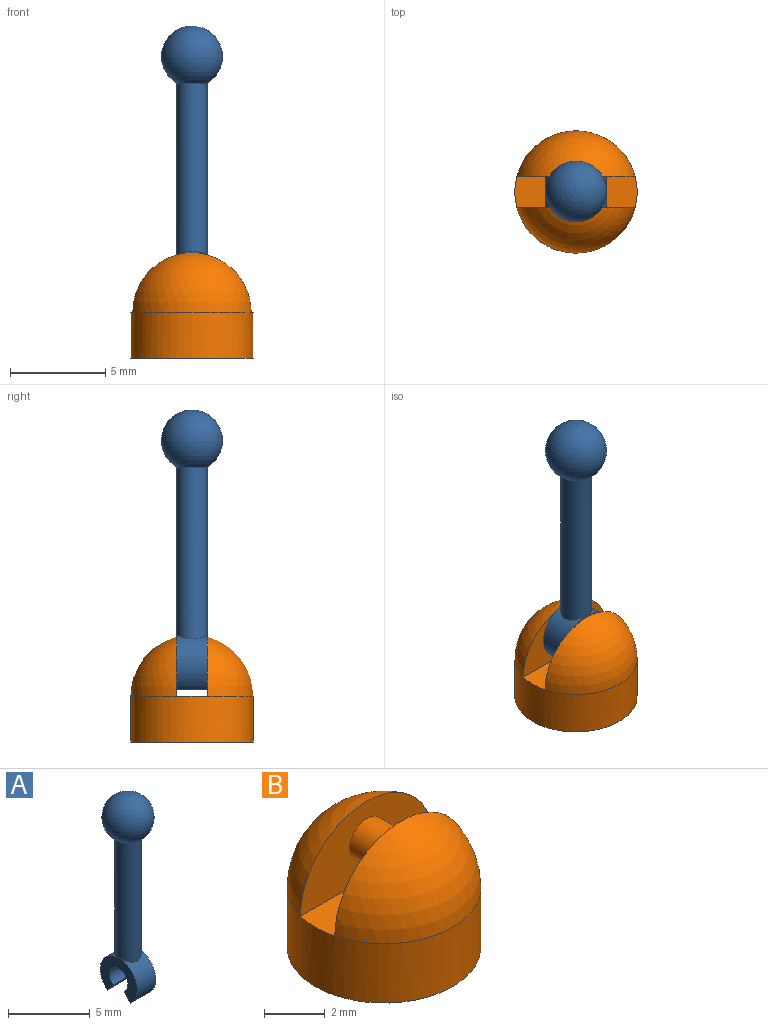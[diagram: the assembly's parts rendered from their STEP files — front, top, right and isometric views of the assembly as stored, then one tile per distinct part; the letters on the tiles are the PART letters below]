
ASSEMBLY  parts=2 mates=1
PART A: 9 faces, bbox 3.2x3.2x14.7 mm
  f0: cylinder r=1.6mm len=2.87mm, axis (-1,0,0), area 5.3mm2, adj f4,f5,f6,f7
  f1: cylinder r=1.6mm len=2.87mm, axis (-1,0,0), area 5.3mm2, adj f2,f5,f6,f7
  f2: plane 1.6x0.63mm, normal (0,0.79,-0.61), area 1.3mm2, adj f1,f3,f5,f6
  f3: cylinder r=0.8mm len=1.6mm, axis (-1,0,0), area 6.4mm2, adj f2,f4,f5,f6
  f4: plane 1.6x0.63mm, normal (0,-0.79,-0.61), area 1.3mm2, adj f0,f3,f5,f6
  f5: plane 3.2x2.87mm, normal (1,0,0), area 4.8mm2, adj f0,f1,f2,f3,f4
  f6: plane 3.2x2.87mm, normal (-1,0,0), area 4.8mm2, adj f0,f1,f2,f3,f4
  f7: cylinder r=0.8mm len=9.01mm, axis (0,0,-1), area 44.8mm2, adj f0,f1,f8
  f8: sphere r=1.6mm, area 30mm2, adj f7
PART B: 10 faces, bbox 6.4x6.4x5.5 mm
  f0: sphere r=3.2mm, area 24.1mm2, adj f1,f4
  f1: cylinder r=3.2mm len=6.4mm, axis (0,0,-1), area 48.3mm2, adj f0,f2,f3,f5
  f2: plane 6.4x6.4mm, normal (0,0,-1), area 14.1mm2, adj f1,f8
  f3: sphere r=3.2mm, area 24.1mm2, adj f1,f6
  f4: plane 6.2x3.1mm, normal (0,1,0), area 13.1mm2, adj f0,f5,f7
  f5: plane 6.4x1.6mm, normal (0,0,1), area 10.1mm2, adj f1,f4,f6
  f6: plane 6.2x3.1mm, normal (0,-1,0), area 13.1mm2, adj f3,f5,f7
  f7: cylinder r=0.8mm len=1.6mm, axis (0,-1,0), area 8mm2, adj f4,f6
  f8: cylinder r=2.4mm len=4.8mm, axis (0,0,-1), area 24.1mm2, adj f2,f9
  f9: plane 4.8x4.8mm, normal (0,0,-1), area 18.1mm2, adj f8
PLACE A rot(axis=(0,0,1),90deg) t=(-1.4,1.02,3.99)mm
PLACE B t=(-1.4,1.02,-0.01)mm fixed
MATE revolute B.f7 <-> A.f3  axis (0,-1,0) through (-1.4,1.02,3.99)mm
